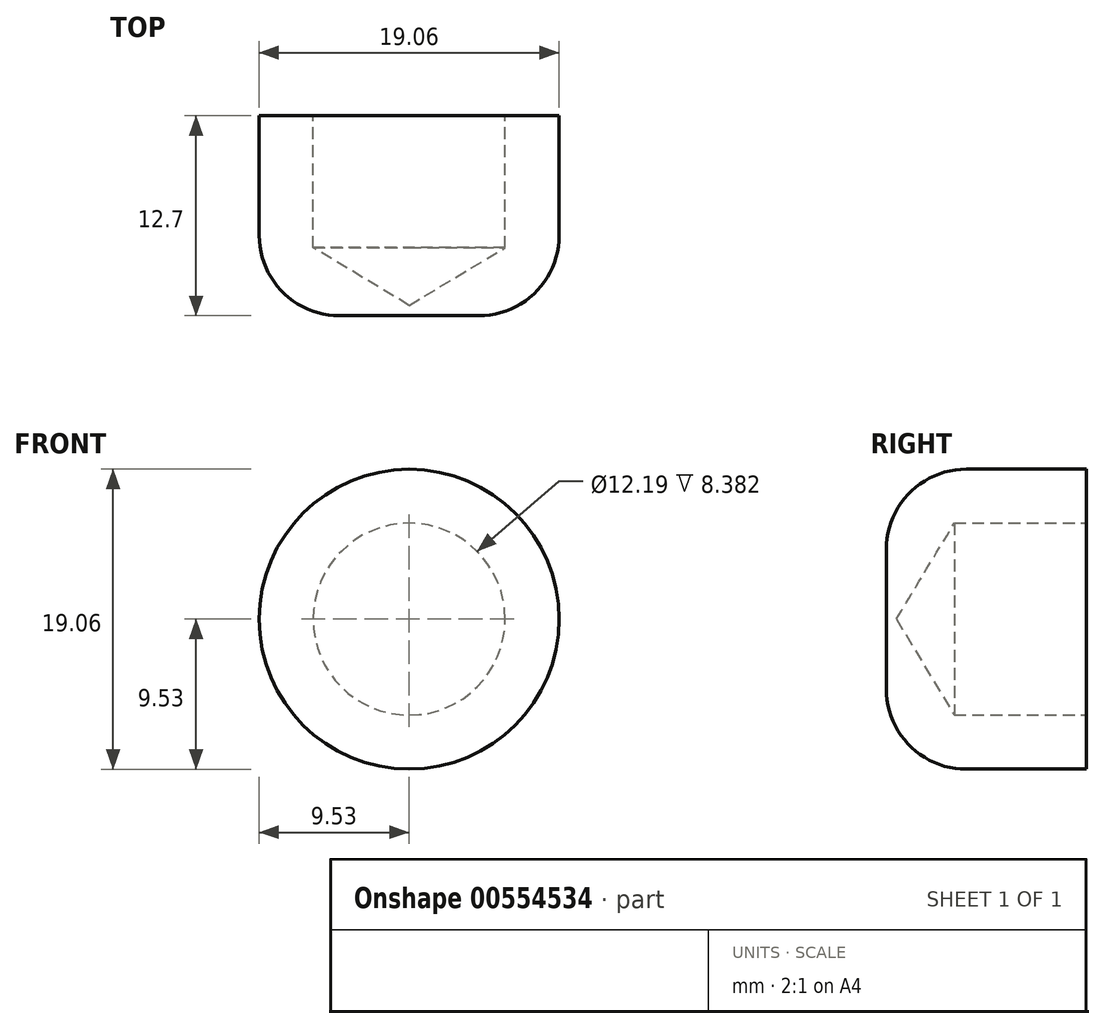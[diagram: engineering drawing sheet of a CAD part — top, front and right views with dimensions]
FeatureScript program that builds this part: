
annotation { "Feature Type Name" : "Feature", "Feature Type Description" : "" }
export const myFeature = defineFeature(function(context is Context, id is Id, definition is map)
    precondition{}
    {
        {
            var Q0;
            Q0=qCreatedBy(makeId("Front.planeOp"),FACE);
            var sketch = newSketch(context, id + "F0", { "sketchPlane" : qUnion([Q0])});
            skPoint(sketch, "E0.middle", {"position": v(0, 0) * mm});
            skCircle(sketch, "E1", {"center": v(0, 0) * mm, "radius": 9.53 * mm});
            skCircle(sketch, "E2", {"center": v(0, 0) * mm, "radius": 6.1 * mm});
            skSolve(sketch);
        }
        {
            var Q0;
            Q0=makeQuery(id+"F0.imprint","IMPRINT",FACE,{"disambiguationData":[TD([[makeQuery(id+"F0.imprint","IMPRINT",EDGE,{"derivedFrom":sQuery(id+"F0.wireOp",EDGE,"E1")}),1.0]])]});
            var Q1;
            Q1=makeQuery(id+"F0.imprint","IMPRINT",FACE,{"disambiguationData":[TD([[makeQuery(id+"F0.imprint","IMPRINT",EDGE,{"derivedFrom":sQuery(id+"F0.wireOp",EDGE,"E2")}),1.0]])]});
            extrude(context, id + "F1", {"entities" : qUnion([Q0, Q1]), "depth" : 12.7 * mm, "offsetDistance" : 25.4 * mm});
        }
        {
            var Q0;
            Q0=makeQuery(id+"F1.opExtrude","CAP_EDGE",EDGE,{"disambiguationData":[OSD([sQuery(id+"F0.wireOp",EDGE,"E1")])],"isStart":false});
            fillet(context, id + "F2", {"entities" : qUnion([Q0]), "radius" : 5.08 * mm, "tangentPropagation" : true, "allowEdgeOverflow" : false});
        }
        {
            var Q0;
            Q0=sQuery(id+"F0.wireOp",VERTEX,"E0.middle");
            var Q1;
            Q1=makeQuery(id+"F1.opExtrude","SWEPT_BODY",BODY,{"disambiguationData":[OSD([sQuery(id+"F0.wireOp",EDGE,"E1")])]});
            hole(context, id + "F3", {"style" : HoleStyle.SIMPLE, "endStyle" : HoleEndStyle.BLIND, "oppositeDirection" : true, "holeDiameter" : 12.2 * mm, "holeDepth" : 8.38 * mm, "isTappedThrough" : true, "tappedDepth" : 12.7 * mm, "tapClearance" : 3, "locations" : qUnion([Q0]), "scope" : qUnion([Q1]), "majorDiameter" : 6.35 * mm});
        }
    });
